# Revit family: Control_Unit-Lutron-Vive_PowPak_CCO_Module
name_source: partatom
category: Lighting Devices
revit_build: Autodesk Revit 2017 (Build: 20160720_1515(x64)
units: mm (PartAtom-declared; Revit-internal decimal feet)

## family parameters
Cut with Voids When Loaded = No
Host = Face
Maintain Annotation Orientation = Yes
OmniClass Number = 23.85.80.11.27
OmniClass Title = Lighting Controls
Part Type = Normal
Room Calculation Point = No
Round Connector Dimension = Use Radius
Shared = No

## types (1)
- RMJS-CCO1-24-B
    Assembly Code = D5020200
    Bracket Offset = 0' - 0 3/16"
    Bracket Thickness = 0' - 0 1/32"
    Bracket Width = 0' - 0 1/4"
    Capacity = 1 A
    Connection Knob = 0' - 0 17/32"
    Connection Knob Diameter = 0' - 0 1/2"
    Connection Knob Radius = 0' - 0 1/4"
    Cost = 0 $
    Current = 1 A
    Default Elevation = 0' - 0"
    Description = Vive PowPak Contact Closure Module
    Device Material = Plastic - Lutron - White
    Edge Radius = 0' - 0 1/4"
    Front Panel Cutout Offset = 0' - 0 9/16"
    Front Panel Left Edge = 0' - 0 11/32"
    Front Panel Right Edge = 0' - 0 11/32"
    Instruction Sheet Link = http://www.lutron.com
    Label 1 = CCO
    Label 2 = 2
    Manufacturer = Lutron Electronics Co., Inc
    Manufacturer Fax Number = 610-282-1243
    Maximum Operating Temperature = 131 °F
    Minimum Operating Temperature = 32 °F
    Model = RMJS-CCO1-24-B
    Number of Poles = 1
    Overall Depth = 0' - 1 1/4"
    Overall Height = 0' - 3 15/32"
    Overall Width = 0' - 2 13/16"
    Performance URL = http://www.lutron.com
    Power = 1 W
    Product Documentation Link = http://www.lutron.com
    Product Name = Vive PowPak CCO Module
    Product Page URL = http://www.lutron.com
    Series = QS
    URL = http://www.lutron.com
    Version = 2017 - v1.0b
    Video Link = https://www.youtube.com
    Voltage = 24 V
    Warranty URL = http://www.lutron.com

## geometry (parser evidence)
native form markers: Sweep x3
no freeform markers — native parametric forms only
